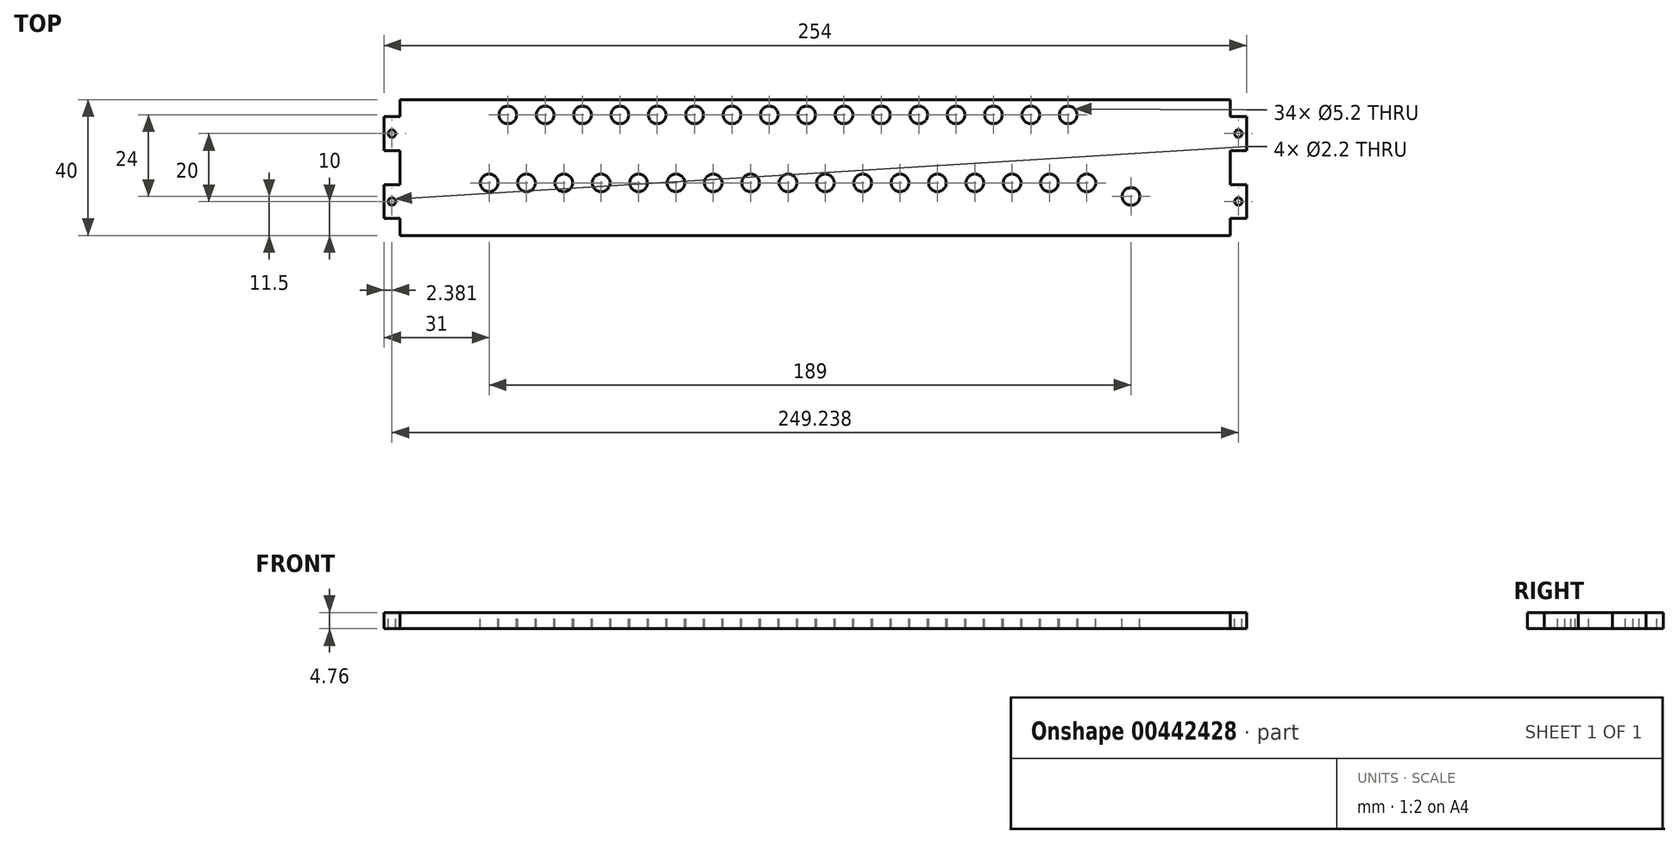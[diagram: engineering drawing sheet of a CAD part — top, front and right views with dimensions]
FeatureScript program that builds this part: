
annotation { "Feature Type Name" : "Feature", "Feature Type Description" : "" }
export const myFeature = defineFeature(function(context is Context, id is Id, definition is map)
    precondition{}
    {
        {
            var Q0;
            Q0=qCreatedBy(makeId("Top.planeOp"),FACE);
            var sketch = newSketch(context, id + "F0", { "sketchPlane" : qUnion([Q0])});
            skLineSegment(sketch, "E0.bottom", {"start": v(-127, 20) * mm, "end": v(127, 20) * mm});
            skLineSegment(sketch, "E0.top", {"start": v(-127, -20) * mm, "end": v(127, -20) * mm});
            skLineSegment(sketch, "E0.left", {"start": v(-127, 20) * mm, "end": v(-127, -20) * mm});
            skLineSegment(sketch, "E0.right", {"start": v(127, 20) * mm, "end": v(127, -20) * mm});
            skPoint(sketch, "E0.middle", {"position": v(0, 0) * mm});
            skSolve(sketch);
        }
        {
            var Q0;
            Q0 = qSketchRegion(id + "F0", true);
            extrude(context, id + "F1", {"entities" : qUnion([Q0]), "depth" : 4.76 * mm});
        }
        {
            var Q0;
            Q0=makeQuery(id+"F1.opExtrude","CAP_FACE",FACE,{"disambiguationData":[OSD([sQuery(id+"F0.wireOp",EDGE,"E0.bottom"),sQuery(id+"F0.wireOp",EDGE,"E0.top"),sQuery(id+"F0.wireOp",EDGE,"E0.left"),sQuery(id+"F0.wireOp",EDGE,"E0.right")])],"isStart":false});
            var sketch = newSketch(context, id + "F2", { "sketchPlane" : qUnion([Q0])});
            skLineSegment(sketch, "E1", {"start": v(0, 0) * mm, "end": v(0, 20) * mm, "construction": true});
            skLineSegment(sketch, "E2", {"start": v(-110, 20) * mm, "end": v(-110, -20) * mm, "construction": true});
            skLineSegment(sketch, "E3", {"start": v(-110, -4.5) * mm, "end": v(127, -4.5) * mm, "construction": true});
            skLineSegment(sketch, "E4", {"start": v(-110, 15.5) * mm, "end": v(127, 15.5) * mm, "construction": true});
            skCircle(sketch, "E5", {"center": v(-96, -4.5) * mm, "radius": 2.6 * mm});
            skCircle(sketch, "E6.1.0.0", {"center": v(-85, -4.5) * mm, "radius": 2.6 * mm});
            skCircle(sketch, "E6.2.0.0", {"center": v(-74, -4.5) * mm, "radius": 2.6 * mm});
            skCircle(sketch, "E6.3.0.0", {"center": v(-63, -4.5) * mm, "radius": 2.6 * mm});
            skCircle(sketch, "E6.4.0.0", {"center": v(-52, -4.5) * mm, "radius": 2.6 * mm});
            skCircle(sketch, "E6.5.0.0", {"center": v(-41, -4.5) * mm, "radius": 2.6 * mm});
            skCircle(sketch, "E6.6.0.0", {"center": v(-30, -4.5) * mm, "radius": 2.6 * mm});
            skCircle(sketch, "E6.7.0.0", {"center": v(-19, -4.5) * mm, "radius": 2.6 * mm});
            skCircle(sketch, "E6.8.0.0", {"center": v(-8, -4.5) * mm, "radius": 2.6 * mm});
            skCircle(sketch, "E6.9.0.0", {"center": v(3, -4.5) * mm, "radius": 2.6 * mm});
            skCircle(sketch, "E6.10.0.0", {"center": v(14, -4.5) * mm, "radius": 2.6 * mm});
            skCircle(sketch, "E6.11.0.0", {"center": v(25, -4.5) * mm, "radius": 2.6 * mm});
            skCircle(sketch, "E6.12.0.0", {"center": v(36, -4.5) * mm, "radius": 2.6 * mm});
            skCircle(sketch, "E6.13.0.0", {"center": v(47, -4.5) * mm, "radius": 2.6 * mm});
            skCircle(sketch, "E6.14.0.0", {"center": v(58, -4.5) * mm, "radius": 2.6 * mm});
            skCircle(sketch, "E6.15.0.0", {"center": v(69, -4.5) * mm, "radius": 2.6 * mm});
            skCircle(sketch, "E6.16.0.0", {"center": v(80, -4.5) * mm, "radius": 2.6 * mm});
            skLineSegment(sketch, "E6.direction1", {"start": v(-96, -4.5) * mm, "end": v(-85, -4.5) * mm, "construction": true});
            skCircle(sketch, "E7", {"center": v(-90.5, 15.5) * mm, "radius": 2.6 * mm});
            skCircle(sketch, "E8.1.0.0", {"center": v(-79.5, 15.5) * mm, "radius": 2.6 * mm});
            skCircle(sketch, "E8.2.0.0", {"center": v(-68.5, 15.5) * mm, "radius": 2.6 * mm});
            skCircle(sketch, "E8.3.0.0", {"center": v(-57.5, 15.5) * mm, "radius": 2.6 * mm});
            skCircle(sketch, "E8.4.0.0", {"center": v(-46.5, 15.5) * mm, "radius": 2.6 * mm});
            skCircle(sketch, "E8.5.0.0", {"center": v(-35.5, 15.5) * mm, "radius": 2.6 * mm});
            skCircle(sketch, "E8.6.0.0", {"center": v(-24.5, 15.5) * mm, "radius": 2.6 * mm});
            skCircle(sketch, "E8.7.0.0", {"center": v(-13.5, 15.5) * mm, "radius": 2.6 * mm});
            skCircle(sketch, "E8.8.0.0", {"center": v(-2.5, 15.5) * mm, "radius": 2.6 * mm});
            skCircle(sketch, "E8.9.0.0", {"center": v(8.5, 15.5) * mm, "radius": 2.6 * mm});
            skCircle(sketch, "E8.10.0.0", {"center": v(19.5, 15.5) * mm, "radius": 2.6 * mm});
            skCircle(sketch, "E8.11.0.0", {"center": v(30.5, 15.5) * mm, "radius": 2.6 * mm});
            skCircle(sketch, "E8.12.0.0", {"center": v(41.5, 15.5) * mm, "radius": 2.6 * mm});
            skCircle(sketch, "E8.13.0.0", {"center": v(52.5, 15.5) * mm, "radius": 2.6 * mm});
            skCircle(sketch, "E8.14.0.0", {"center": v(63.5, 15.5) * mm, "radius": 2.6 * mm});
            skCircle(sketch, "E8.15.0.0", {"center": v(74.5, 15.5) * mm, "radius": 2.6 * mm});
            skLineSegment(sketch, "E8.direction1", {"start": v(-90.5, 15.5) * mm, "end": v(-79.5, 15.5) * mm, "construction": true});
            skCircle(sketch, "E9", {"center": v(93, -8.5) * mm, "radius": 2.6 * mm});
            skSolve(sketch);
        }
        {
            var Q0;
            Q0 = qSketchRegion(id + "F2", true);
            extrude(context, id + "F3", {"entities" : qUnion([Q0]), "operationType" : NewBodyOperationType.REMOVE, "oppositeDirection" : true, "depth" : 25.4 * mm});
        }
        {
            var Q0;
            Q0=makeQuery(id+"F1.opExtrude","CAP_FACE",FACE,{"disambiguationData":[OSD([sQuery(id+"F0.wireOp",EDGE,"E0.bottom"),sQuery(id+"F0.wireOp",EDGE,"E0.top"),sQuery(id+"F0.wireOp",EDGE,"E0.left"),sQuery(id+"F0.wireOp",EDGE,"E0.right")])],"isStart":false});
            var sketch = newSketch(context, id + "F4", { "sketchPlane" : qUnion([Q0])});
            skLineSegment(sketch, "E10", {"start": v(-127, 0) * mm, "end": v(-165.3, 0) * mm, "construction": true});
            skPoint(sketch, "E10.endSnap0", {"position": v(-127, 0) * mm});
            skLineSegment(sketch, "E11", {"start": v(-127, 15) * mm, "end": v(-122.24, 15) * mm, "construction": true});
            skLineSegment(sketch, "E12", {"start": v(-122.24, 15) * mm, "end": v(-122.24, 5) * mm, "construction": true});
            skLineSegment(sketch, "E13", {"start": v(-122.24, 5) * mm, "end": v(-127, 5) * mm, "construction": true});
            skLineSegment(sketch, "E14", {"start": v(-127, 5) * mm, "end": v(-127, 15) * mm, "construction": true});
            skLineSegment(sketch, "E15", {"start": v(-127, 10) * mm, "end": v(-122.24, 10) * mm, "construction": true});
            skLineSegment(sketch, "E16", {"start": v(-127, 15) * mm, "end": v(-127, 20) * mm});
            skLineSegment(sketch, "E17", {"start": v(-127, 20) * mm, "end": v(-122.24, 20) * mm});
            skLineSegment(sketch, "E18", {"start": v(-122.24, 20) * mm, "end": v(-122.24, 15) * mm});
            skLineSegment(sketch, "E19", {"start": v(-127, 0) * mm, "end": v(-127, 5) * mm});
            skLineSegment(sketch, "E20", {"start": v(-122.24, 5) * mm, "end": v(-122.24, 0) * mm});
            skLineSegment(sketch, "E21.MirrorCS", {"start": v(-127, -15) * mm, "end": v(-127, -20) * mm});
            skLineSegment(sketch, "E22.MirrorCS", {"start": v(-127, -20) * mm, "end": v(-122.24, -20) * mm});
            skLineSegment(sketch, "E23.MirrorCS", {"start": v(-122.24, -20) * mm, "end": v(-122.24, -15) * mm});
            skLineSegment(sketch, "E24.MirrorCS", {"start": v(-122.24, -5) * mm, "end": v(-127, -5) * mm, "construction": true});
            skLineSegment(sketch, "E25.MirrorCS", {"start": v(-127, 0) * mm, "end": v(-127, -5) * mm});
            skLineSegment(sketch, "E26.MirrorCS", {"start": v(-122.24, -5) * mm, "end": v(-122.24, 0) * mm});
            skLineSegment(sketch, "E27", {"start": v(-127, -5) * mm, "end": v(-122.24, -5) * mm});
            skLineSegment(sketch, "E28", {"start": v(-122.24, -15) * mm, "end": v(-127, -15) * mm});
            skLineSegment(sketch, "E29", {"start": v(-127, 15) * mm, "end": v(-122.24, 15) * mm});
            skLineSegment(sketch, "E30", {"start": v(0, 0) * mm, "end": v(0, 33.03) * mm, "construction": true});
            skLineSegment(sketch, "E31.MirrorCS", {"start": v(122.24, 20) * mm, "end": v(122.24, 15) * mm});
            skLineSegment(sketch, "E32.MirrorCS", {"start": v(127, 20) * mm, "end": v(122.24, 20) * mm});
            skLineSegment(sketch, "E33.MirrorCS", {"start": v(127, 15) * mm, "end": v(127, 20) * mm});
            skLineSegment(sketch, "E34.MirrorCS", {"start": v(127, 15) * mm, "end": v(122.24, 15) * mm, "construction": true});
            skLineSegment(sketch, "E35", {"start": v(-127, 5) * mm, "end": v(-127, -5) * mm});
            skLineSegment(sketch, "E36", {"start": v(-127, 5) * mm, "end": v(-122.24, 5) * mm});
            skLineSegment(sketch, "E37.MirrorCS", {"start": v(127, 0) * mm, "end": v(127, 5) * mm});
            skLineSegment(sketch, "E38.MirrorCS", {"start": v(127, 0) * mm, "end": v(127, -5) * mm});
            skLineSegment(sketch, "E39.MirrorCS", {"start": v(122.24, -5) * mm, "end": v(127, -5) * mm, "construction": true});
            skLineSegment(sketch, "E40.MirrorCS", {"start": v(122.24, -5) * mm, "end": v(122.24, 0) * mm});
            skLineSegment(sketch, "E41.MirrorCS", {"start": v(122.24, 5) * mm, "end": v(122.24, 0) * mm});
            skLineSegment(sketch, "E42.MirrorCS", {"start": v(122.24, -15) * mm, "end": v(127, -15) * mm});
            skLineSegment(sketch, "E43.MirrorCS", {"start": v(127, -15) * mm, "end": v(127, -20) * mm});
            skLineSegment(sketch, "E44.MirrorCS", {"start": v(127, -20) * mm, "end": v(122.24, -20) * mm});
            skLineSegment(sketch, "E45.MirrorCS", {"start": v(122.24, -20) * mm, "end": v(122.24, -15) * mm});
            skLineSegment(sketch, "E46", {"start": v(122.24, 15) * mm, "end": v(127, 15) * mm});
            skLineSegment(sketch, "E47", {"start": v(122.24, 5) * mm, "end": v(127, 5) * mm});
            skLineSegment(sketch, "E48", {"start": v(122.24, -5) * mm, "end": v(127, -5) * mm});
            skSolve(sketch);
        }
        {
            var Q0;
            Q0 = qSketchRegion(id + "F4", true);
            extrude(context, id + "F5", {"entities" : qUnion([Q0]), "operationType" : NewBodyOperationType.REMOVE, "oppositeDirection" : true, "depth" : 25.4 * mm});
        }
        {
            var Q0;
            Q0=makeQuery(id+"F1.opExtrude","CAP_FACE",FACE,{"disambiguationData":[OSD([sQuery(id+"F0.wireOp",EDGE,"E0.bottom"),sQuery(id+"F0.wireOp",EDGE,"E0.top"),sQuery(id+"F0.wireOp",EDGE,"E0.left"),sQuery(id+"F0.wireOp",EDGE,"E0.right")])],"isStart":false});
            var sketch = newSketch(context, id + "F6", { "sketchPlane" : qUnion([Q0])});
            skCircle(sketch, "E49", {"center": v(124.62, 10) * mm, "radius": 1.1 * mm});
            skPoint(sketch, "E49.centerSnap0", {"position": v(127, 10) * mm});
            skLineSegment(sketch, "E50", {"start": v(122.24, 0) * mm, "end": v(126.94, 0) * mm, "construction": true});
            skCircle(sketch, "E51.MirrorC", {"center": v(124.62, -10) * mm, "radius": 1.1 * mm});
            skLineSegment(sketch, "E52", {"start": v(0, 0) * mm, "end": v(0, 38.74) * mm, "construction": true});
            skCircle(sketch, "E53.MirrorC", {"center": v(-124.62, -10) * mm, "radius": 1.1 * mm});
            skCircle(sketch, "E54.MirrorC", {"center": v(-124.62, 10) * mm, "radius": 1.1 * mm});
            skSolve(sketch);
        }
        {
            var Q0;
            Q0 = qSketchRegion(id + "F6", true);
            extrude(context, id + "F7", {"entities" : qUnion([Q0]), "operationType" : NewBodyOperationType.REMOVE, "oppositeDirection" : true, "depth" : 25.4 * mm});
        }
    });
